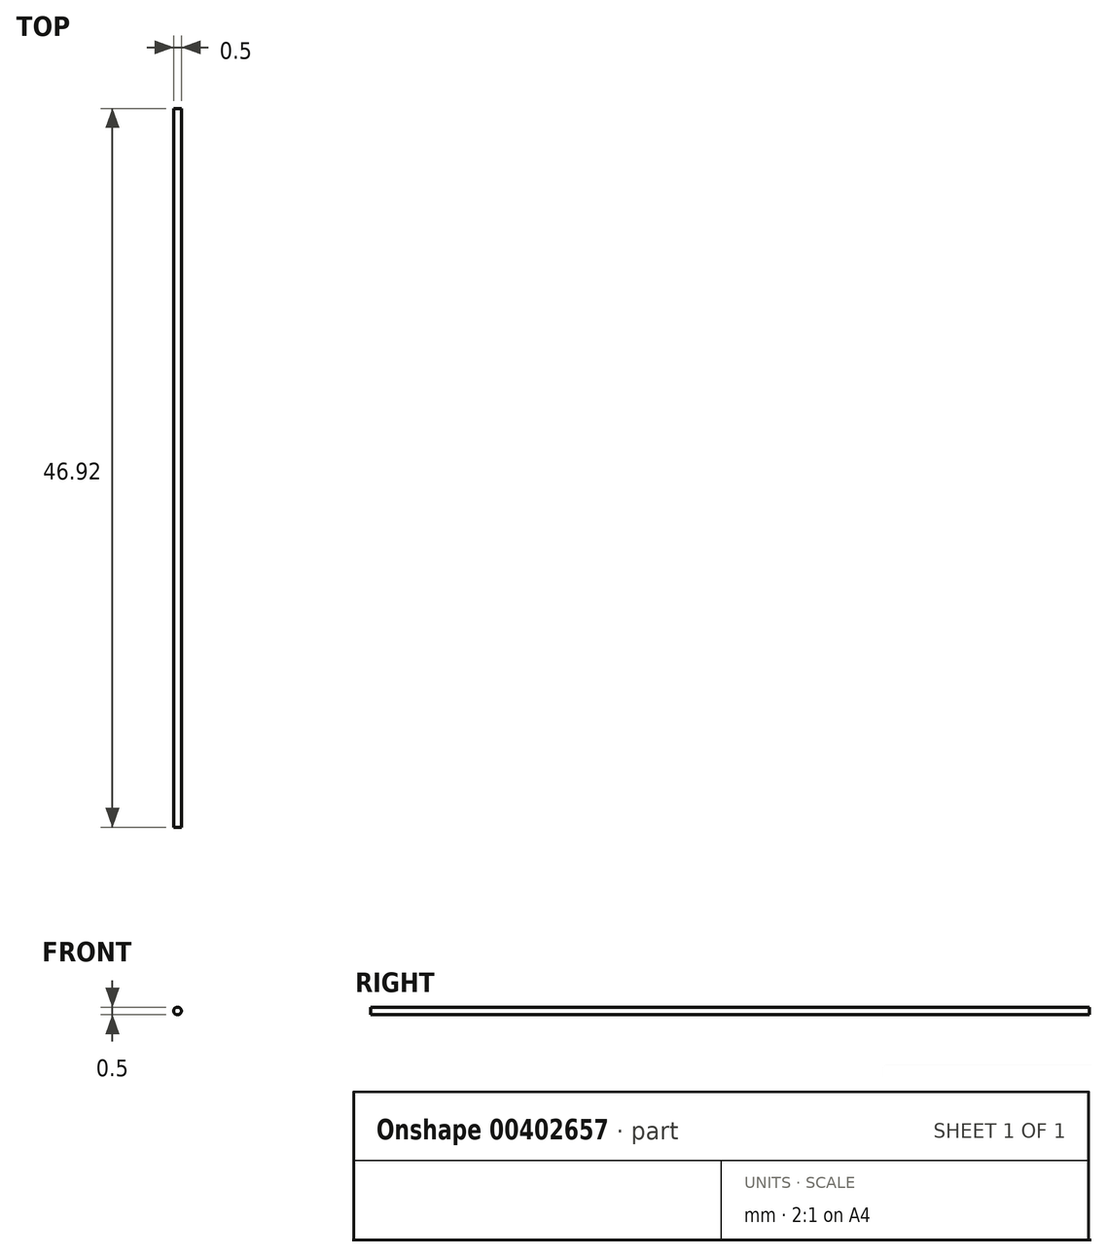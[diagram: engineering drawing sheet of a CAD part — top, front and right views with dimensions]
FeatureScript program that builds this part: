
annotation { "Feature Type Name" : "Feature", "Feature Type Description" : "" }
export const myFeature = defineFeature(function(context is Context, id is Id, definition is map)
    precondition{}
    {
        {
            var Q0;
            Q0=qCreatedBy(makeId("Front.planeOp"),FACE);
            var sketch = newSketch(context, id + "F0", { "sketchPlane" : qUnion([Q0])});
            skCircle(sketch, "E0", {"center": v(0, 0) * mm, "radius": 0.25 * mm});
            skSolve(sketch);
        }
        {
            var Q0;
            Q0=qCreatedBy(makeId("Top.planeOp"),FACE);
            var sketch = newSketch(context, id + "F1", { "sketchPlane" : qUnion([Q0])});
            skLineSegment(sketch, "E1", {"start": v(0, 0) * mm, "end": v(0, 46.92) * mm});
            skSolve(sketch);
        }
        {
            var Q0;
            Q0=makeQuery(id+"F0.imprint","IMPRINT",FACE,{"disambiguationData":[TD([[makeQuery(id+"F0.imprint","IMPRINT",EDGE,{"derivedFrom":sQuery(id+"F0.wireOp",EDGE,"E0")}),1.0]])]});
            var Q1;
            Q1=sQuery(id+"F1.wireOp",EDGE,"E1");
            sweep(context, id + "F2", {"profiles" : qUnion([Q0]), "path" : qUnion([Q1])});
        }
    });
